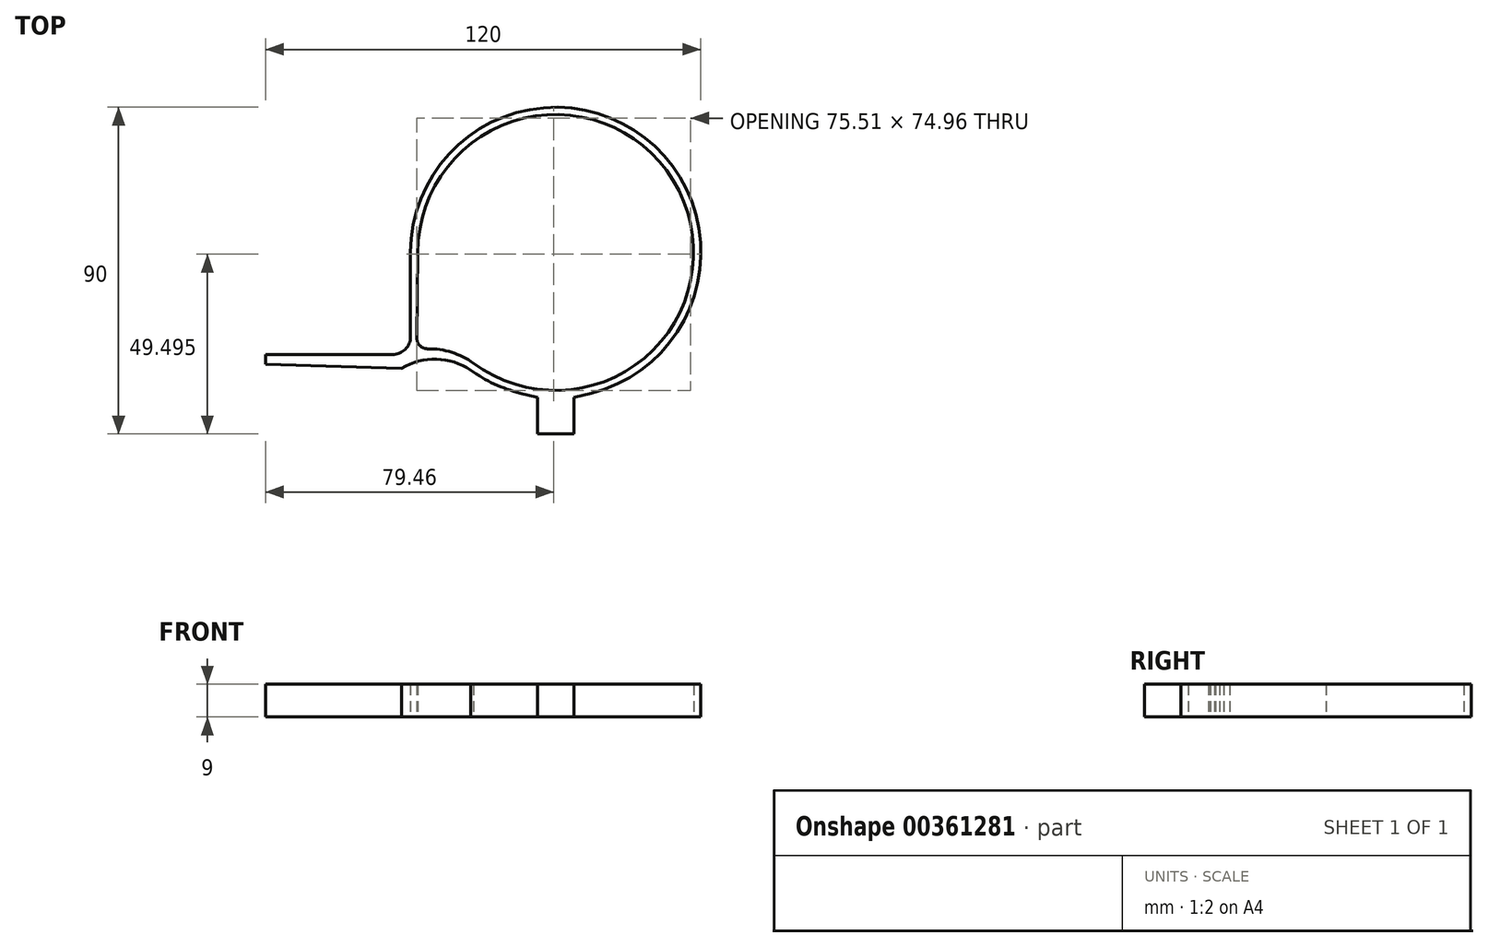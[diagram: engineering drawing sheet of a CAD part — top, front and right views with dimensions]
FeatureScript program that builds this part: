
annotation { "Feature Type Name" : "Feature", "Feature Type Description" : "" }
export const myFeature = defineFeature(function(context is Context, id is Id, definition is map)
    precondition{}
    {
        {
            var Q0;
            Q0=qCreatedBy(makeId("Top.planeOp"),FACE);
            var sketch = newSketch(context, id + "F0", { "sketchPlane" : qUnion([Q0])});
            skLineSegment(sketch, "E0", {"start": v(-5, -40) * mm, "end": v(-5, -50) * mm});
            skLineSegment(sketch, "E1", {"start": v(-5, -50) * mm, "end": v(5, -50) * mm});
            skLineSegment(sketch, "E2", {"start": v(5, -50) * mm, "end": v(5, -40) * mm});
            skLineSegment(sketch, "E3", {"start": v(5, -40) * mm, "end": v(9.85, -38.77) * mm});
            skLineSegment(sketch, "E4", {"start": v(-38, 0) * mm, "end": v(-38.3, -23.52) * mm});
            skLineSegment(sketch, "E5", {"start": v(-40, 0) * mm, "end": v(-40, -23.16) * mm});
            skLineSegment(sketch, "E6.trimOffspring", {"start": v(-5, -40) * mm, "end": v(-67.43, -40) * mm, "construction": true});
            skLineSegment(sketch, "E7", {"start": v(-5, -40) * mm, "end": v(-5, -35.3) * mm, "construction": true});
            skLineSegment(sketch, "E8", {"start": v(-40, -30.75) * mm, "end": v(-39.87, -30.66) * mm, "construction": true});
            skPoint(sketch, "E9.orphan", {"position": v(-37.98, -30.8) * mm});
            skPoint(sketch, "E10.trimOffspring.end.orphan", {"position": v(-40, -56.58) * mm});
            skPoint(sketch, "E11.trimOffspring.end.orphan", {"position": v(-38.5, -56.58) * mm});
            skPoint(sketch, "E12.visualSharp", {"position": v(-38.24, -29.33) * mm});
            skPoint(sketch, "E13.visualSharp", {"position": v(-40, -25.25) * mm});
            skLineSegment(sketch, "E13.filletArc", {"start": v(-40, -25.25) * mm, "end": v(-40, -25.25) * mm});
            skPoint(sketch, "E14.visualSharp", {"position": v(-34.65, -32.17) * mm});
            skArc(sketch, "E15", {"start": v(-22.67, -30.5) * mm, "mid": v(33.95, 17.06) * mm, "end": v(-38, 0) * mm});
            skLineSegment(sketch, "E16", {"start": v(-40, -25.25) * mm, "end": v(-40, -39.6) * mm, "construction": true});
            skPoint(sketch, "E17.second.point", {"position": v(-27.2, -29.33) * mm});
            skPoint(sketch, "E17.third.point", {"position": v(-35, -27.47) * mm});
            skPoint(sketch, "E18.first.point", {"position": v(-25.93, -27.78) * mm});
            skPoint(sketch, "E18.second.point", {"position": v(-38.24, -27.47) * mm});
            skPoint(sketch, "E18.third.point", {"position": v(-32, -25.3) * mm});
            skLineSegment(sketch, "E19", {"start": v(-45, -28.16) * mm, "end": v(-80, -28.16) * mm});
            skLineSegment(sketch, "E20", {"start": v(-42.43, -31.92) * mm, "end": v(-80, -30.75) * mm});
            skLineSegment(sketch, "E21", {"start": v(-80, -30.75) * mm, "end": v(-80, -28.16) * mm});
            skPoint(sketch, "E22.newPointA", {"position": v(-40, -28.16) * mm});
            skArc(sketch, "E22.filletArc", {"start": v(-40, -25.25) * mm, "mid": v(-40, -25.2) * mm, "end": v(-40, -25.16) * mm});
            skPoint(sketch, "E23.visualSharp", {"position": v(-40, -32) * mm});
            skArc(sketch, "E24.trimOffspring", {"start": v(9.85, -38.77) * mm, "mid": v(24.56, 31.57) * mm, "end": v(-40, 0) * mm});
            skLineSegment(sketch, "E25", {"start": v(-5, -40) * mm, "end": v(-9.85, -38.77) * mm});
            skArc(sketch, "E26", {"start": v(-23.42, -32.43) * mm, "mid": v(-32.85, -29.41) * mm, "end": v(-42.43, -31.92) * mm});
            skPoint(sketch, "E26.second.point", {"position": v(-23.42, -32.43) * mm});
            skPoint(sketch, "E26.second.point.positionSnap0", {"position": v(-40, -32.43) * mm});
            skPoint(sketch, "E26.third.point", {"position": v(-33.05, -29.4) * mm});
            skArc(sketch, "E27.trimOffspring", {"start": v(-23.42, -32.43) * mm, "mid": v(-16.93, -36.24) * mm, "end": v(-9.85, -38.77) * mm});
            skArc(sketch, "E28", {"start": v(-22.29, -30.78) * mm, "mid": v(-28.42, -27.6) * mm, "end": v(-35.25, -26.56) * mm});
            skPoint(sketch, "E28.second.point", {"position": v(-22.29, -30.78) * mm});
            skPoint(sketch, "E28.third.point", {"position": v(-34.23, -26.57) * mm});
            skArc(sketch, "E29.filletArc", {"start": v(-45, -28.16) * mm, "mid": v(-41.46, -26.7) * mm, "end": v(-40, -23.16) * mm});
            skPoint(sketch, "E30.orphan", {"position": v(-38.5, -39.6) * mm});
            skPoint(sketch, "E31.trimOffspring.end.orphan", {"position": v(-38.37, -29.56) * mm});
            skPoint(sketch, "E32.end.orphan", {"position": v(-38.37, -31.4) * mm});
            skPoint(sketch, "E33.visualSharp", {"position": v(-38.34, -26.83) * mm});
            skArc(sketch, "E33.filletArc", {"start": v(-38.3, -23.52) * mm, "mid": v(-37.42, -25.68) * mm, "end": v(-35.25, -26.56) * mm});
            skLineSegment(sketch, "E34", {"start": v(-5, -40) * mm, "end": v(5, -40) * mm, "construction": true});
            skSolve(sketch);
        }
        {
            var Q0;
            Q0=makeQuery(id+"F0.imprint","IMPRINT",FACE,{"disambiguationData":[TD([[makeQuery(id+"F0.imprint","IMPRINT",EDGE,{"derivedFrom":sQuery(id+"F0.wireOp",EDGE,"E4")}),-1.0]])]});
            extrude(context, id + "F1", {"entities" : qUnion([Q0]), "depth" : 9 * mm});
        }
    });
